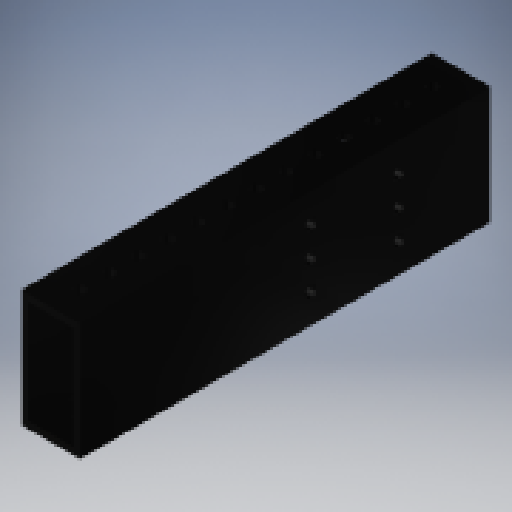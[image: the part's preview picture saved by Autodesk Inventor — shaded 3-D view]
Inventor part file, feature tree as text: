
AUTODESK INVENTOR PART (.ipt)
format: ipt  version: 2024.2 (Build 282272000, 272)  size: 757,248 bytes
history: native  units: in
note: dims shown in document units (in); Inventor stores cm internally (conversion verified against a paired STEP export)
features: other x13, extrude x10, hole x3, pattern_linear x3, mirror x3, sketch x2, sheet_metal_op x1, plane x1
ambient origin geometry x8: Origin, YZ Plane, XZ Plane, XY Plane, X Axis, Y Axis, Z Axis, Center Point
bodies: Solid1 (feature_tree)
feature tree (36):
  other  "Blocks"
  other  "Base Sketch"
  extrude  "Base"  Depth=1.0in
  extrude  "MAX Corner"  Depth=0.125in
  extrude  "MAX Corner Cut"  Depth=1.0in
  extrude  "Scribe Lines"  Depth=1.0in
  other  "Side Middle"
  other  "Top Middle"
  other  "Side Holes Sketch"
  hole  "Top Side Hole"  [1 undecoded]
  hole  "Mid Side Hole"  [1 undecoded]
  hole  "Btm Side Hole"  [1 undecoded]
  pattern_linear  "Side Holes"  Spacing1=7.0in  [1 undecoded]
  mirror  "Side Mirror"
  extrude  "MAXTube Hole"  TaperAngle=0.0deg  [1 undecoded]
  extrude  "MAXTube Outside"  Depth=7.0in
  pattern_linear  "MAXTube Pattern"  Spacing1=0.0in  [1 undecoded]
  mirror  "MAXTube Mirror"
  extrude  "Left Top Hole"  TaperAngle=0.0deg  [1 undecoded]
  extrude  "Mid Top Hole"  Depth=1.0in
  extrude  "Right Top Hole"  TaperAngle=0.0deg  [1 undecoded]
  pattern_linear  "Top Holes"  Spacing1=0.5in  [1 undecoded]
  mirror  "Top Mirror"
  extrude  "Extrusion14"  Depth=1.0in
  sketch  "Sketch9"  dims[d2=0.125in d3=0.125in d4=0.4375in d5=0.04in d6=0.0671in d7=0.0272in d8=0.0in d9=0.0in d10=0.0in d11=0.085in d12=0.085in d16=0.04in d17=0.04in d18=0.04in d19=0.04in d20=7.0in d21=0.0in d22=7.0in d23=0.0in d24=0.0in d25=0.0in d26=0.005in d30=0.0in d31=0.0in d34=0.5in d35=0.5in d38=0.5in d40=0.196in d41=0.75in d42=0.375in d43=0.25in d44=0.5635in d45=1.0in d46=0.8108in d47=0.196in d48=0.75in d49=0.375in d50=0.25in d51=0.5635in d52=1.0in d53=0.8108in d54=0.196in d55=0.75in d56=0.375in d57=0.25in d58=0.5635in d59=1.0in d60=0.8108in d61=0.5in d62=0.3937in d64=0.5in d69=1.5in d70=0.0in d71=0.0in d72=0.7874in d74=2.0in d78=2.0in d79=-3.5in d80=0.196in d81=0.0in d82=0.0in d83=0.5in d84=0.0in d85=0.0in d86=0.0in d87=0.0in d88=0.0in d89=0.0in d90=2.7559in d92=0.5in d93=1.0in d95=0.0in d96=0.0in d97=1.5in d98=4.0in d100=-3.5in d187=1.375in d188=0.0in d193=0.7874in d195=0.5in d196=0.7874in d198=0.5in d209=0.196in d210=0.5in d212=0.5in d213=3.07in d214=1.5in]
  sheet_metal_op  "Corner"
  other  "MAXTube"
  plane  "Work Plane3"
  sketch  "Sketch7"  dims[d0=2.0in d1=1.0in]
  other  "Corner:5"
  other  "Corner:6"
  other  "Corner:7"
  other  "Corner:8"
  other  "MAXTube:1"
  other  "MAXTube:2"
  other  "MAXTube:3"
note: 9 required parameter values undecoded (feature->parameter linkage not recoverable at this tier; creation-order binding heuristic only, values carry confidence <= 0.55)
